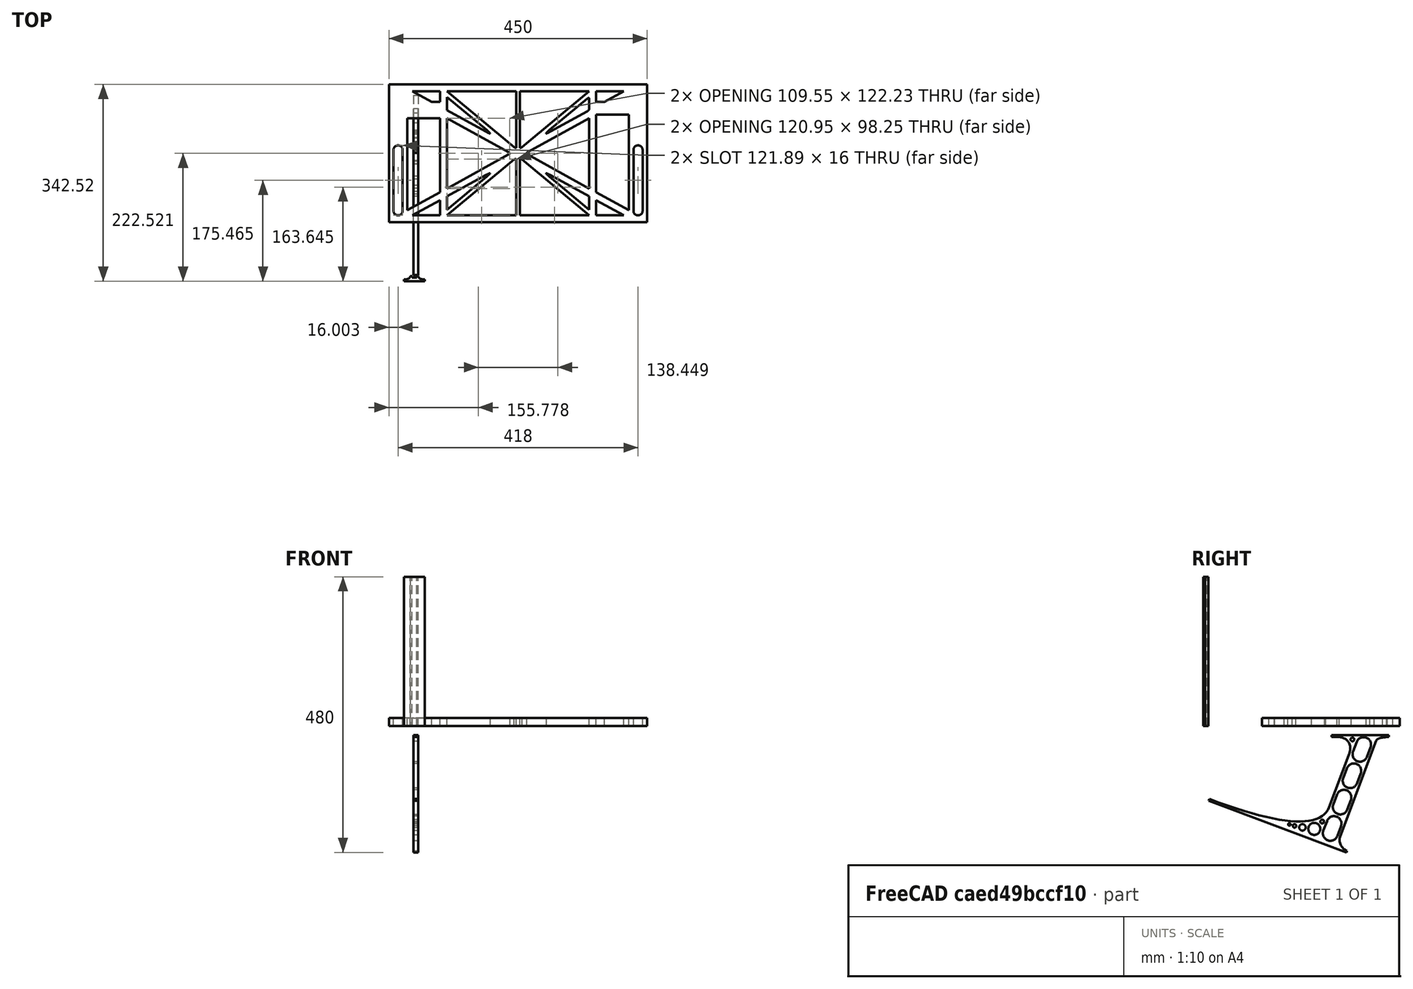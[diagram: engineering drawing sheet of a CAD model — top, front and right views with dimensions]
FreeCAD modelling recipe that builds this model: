
FCSTD DOCUMENT  (FreeCAD 0.19R0.19.2)
Label: laptopStand071
License: All rights reserved
LicenseURL: http://en.wikipedia.org/wiki/All_rights_reserved
objects: Sketcher::SketchObject×3, Part::Extrusion×3
note: 6 computed .brp shape members not serialized (recipe doc carries the construction recipe); baked Part::Feature solids carry a one-line shape summary decoded from their .brp

FEATURE [Sketcher::SketchObject] Sketch
  FullyConstrained = true
  sketch-geometry (136):
    g0: LineSegment StartX=-10.9272 StartY=-82.7794 StartZ=0 EndX=46.0728 EndY=-51.4823 EndZ=0
    g1: LineSegment StartX=366.073 StartY=-91.7794 StartZ=0 EndX=318.073 EndY=-65.424 EndZ=0
    g2: LineSegment StartX=-10.9272 StartY=77.3346 StartZ=0 EndX=-10.9272 EndY=-82.7794 EndZ=0
    g3: LineSegment StartX=375.073 StartY=-82.7794 StartZ=0 EndX=375.073 EndY=83.9235 EndZ=0
    g4: LineSegment StartX=-1.92719 StartY=-91.7794 StartZ=0 EndX=46.0728 EndY=-91.7794 EndZ=0
    g5: LineSegment StartX=318.073 StartY=124.221 StartZ=0 EndX=366.073 EndY=124.221 EndZ=0
    g6: LineSegment StartX=306.073 StartY=124.221 StartZ=0 EndX=189.124 EndY=27.0628 EndZ=0
    g7: LineSegment StartX=58.0728 StartY=-91.7794 StartZ=0 EndX=175.022 EndY=5.37834 EndZ=0
    g8: LineSegment StartX=58.0728 StartY=-81.8102 StartZ=0 EndX=58.0728 EndY=-58.8351 EndZ=0
    g9: LineSegment StartX=175.022 StartY=27.0628 StartZ=0 EndX=58.0728 EndY=124.221 EndZ=0
    g10: LineSegment StartX=189.124 StartY=5.37834 StartZ=0 EndX=306.073 EndY=-91.7794 EndZ=0
    g11: LineSegment StartX=306.073 StartY=77.3346 StartZ=0 EndX=306.073 EndY=-44.8935 EndZ=0
    g12: LineSegment StartX=318.073 StartY=83.9235 StartZ=0 EndX=318.073 EndY=-51.4823 EndZ=0
    g13: LineSegment StartX=306.073 StartY=-58.8351 StartZ=0 EndX=306.073 EndY=-81.8102 EndZ=0
    g14: LineSegment StartX=318.073 StartY=-51.4823 StartZ=0 EndX=375.073 EndY=-82.7794 EndZ=0
    g15: LineSegment StartX=318.073 StartY=-65.424 StartZ=0 EndX=318.073 EndY=-91.7794 EndZ=0
    g16: LineSegment StartX=318.073 StartY=-91.7794 StartZ=0 EndX=366.073 EndY=-91.7794 EndZ=0
    g17: LineSegment StartX=58.0728 StartY=-44.8935 StartZ=0 EndX=58.0728 EndY=77.3346 EndZ=0
    g18: LineSegment StartX=46.0728 StartY=-65.424 StartZ=0 EndX=-1.92719 EndY=-91.7794 EndZ=0
    g19: LineSegment StartX=46.0728 StartY=-65.424 StartZ=0 EndX=46.0728 EndY=-91.7794 EndZ=0
    g20: LineSegment StartX=58.0728 StartY=91.2763 StartZ=0 EndX=58.0728 EndY=114.251 EndZ=0
    g21: LineSegment StartX=46.0728 StartY=77.3346 StartZ=0 EndX=46.0728 EndY=-51.4823 EndZ=0
    g22: LineSegment StartX=-42.9272 StartY=136.221 StartZ=0 EndX=-42.9272 EndY=-103.779 EndZ=0
    g23: LineSegment StartX=407.073 StartY=136.221 StartZ=0 EndX=407.073 EndY=-103.779 EndZ=0
    g24: LineSegment StartX=179.022 StartY=27.0628 StartZ=0 EndX=179.022 EndY=124.221 EndZ=0
    g25: LineSegment StartX=185.124 StartY=27.0628 StartZ=0 EndX=185.124 EndY=124.221 EndZ=0
    g26: ArcOfCircle CenterX=-26.9272 CenterY=22.1087 CenterZ=0 NormalX=0 NormalY=0 NormalZ=1 AngleXU=0 Radius=8 StartAngle=1e-16 EndAngle=3.14159
    g27: ArcOfCircle CenterX=-26.9272 CenterY=-83.7794 CenterZ=0 NormalX=0 NormalY=0 NormalZ=1 AngleXU=0 Radius=8 StartAngle=3.14159 EndAngle=6.28319
    g28: LineSegment StartX=-34.9272 StartY=22.1087 StartZ=0 EndX=-34.9272 EndY=-83.7794 EndZ=0
    g29: LineSegment StartX=-18.9272 StartY=22.1087 StartZ=0 EndX=-18.9272 EndY=-83.7794 EndZ=0
    g30: LineSegment StartX=185.124 StartY=-91.7794 StartZ=0 EndX=306.073 EndY=-91.7794 EndZ=0
    g31: LineSegment StartX=179.022 StartY=-91.7794 StartZ=0 EndX=58.0728 EndY=-91.7794 EndZ=0
    g32: LineSegment StartX=306.073 StartY=124.221 StartZ=0 EndX=185.124 EndY=124.221 EndZ=0
    g33: LineSegment StartX=179.022 StartY=124.221 StartZ=0 EndX=58.0728 EndY=124.221 EndZ=0
    g34: ArcOfCircle CenterX=391.073 CenterY=22.1087 CenterZ=0 NormalX=0 NormalY=0 NormalZ=1 AngleXU=0 Radius=8 StartAngle=-4.4e-15 EndAngle=3.14159
    g35: LineSegment StartX=399.073 StartY=22.1087 StartZ=0 EndX=399.073 EndY=-83.7794 EndZ=0
    g36: LineSegment StartX=383.073 StartY=22.1087 StartZ=0 EndX=383.073 EndY=-83.7794 EndZ=0
    g37: ArcOfCircle CenterX=391.073 CenterY=-83.7794 CenterZ=0 NormalX=0 NormalY=0 NormalZ=1 AngleXU=0 Radius=8 StartAngle=3.14159 EndAngle=6.28319
    g38: Circle CenterX=175.022 CenterY=27.0628 CenterZ=0 NormalX=0 NormalY=0 NormalZ=1 AngleXU=0 Radius=1
    g39: Circle CenterX=179.022 CenterY=24.8665 CenterZ=0 NormalX=0 NormalY=0 NormalZ=1 AngleXU=0 Radius=1
    g40: Circle CenterX=179.022 CenterY=27.0628 CenterZ=0 NormalX=0 NormalY=0 NormalZ=1 AngleXU=0 Radius=1
    g41: BSplineCurve PolesCount=3 KnotsCount=2 Degree=2 IsPeriodic=0
    g42: GeomPoint X=175.022 Y=27.0628 Z=0
    g43: GeomPoint X=179.022 Y=27.0628 Z=0
    g44: Circle CenterX=189.124 CenterY=27.0628 CenterZ=0 NormalX=0 NormalY=0 NormalZ=1 AngleXU=0 Radius=1
    g45: Circle CenterX=185.124 CenterY=24.8665 CenterZ=0 NormalX=0 NormalY=0 NormalZ=1 AngleXU=0 Radius=1
    g46: Circle CenterX=185.124 CenterY=27.0628 CenterZ=0 NormalX=0 NormalY=0 NormalZ=1 AngleXU=0 Radius=1
    g47: BSplineCurve PolesCount=3 KnotsCount=2 Degree=2 IsPeriodic=0
    g48: GeomPoint X=189.124 Y=27.0628 Z=0
    g49: GeomPoint X=185.124 Y=27.0628 Z=0
    g50: Circle CenterX=175.022 CenterY=5.37834 CenterZ=0 NormalX=0 NormalY=0 NormalZ=1 AngleXU=0 Radius=1
    g51: Circle CenterX=179.022 CenterY=7.57463 CenterZ=0 NormalX=0 NormalY=0 NormalZ=1 AngleXU=0 Radius=1
    g52: Circle CenterX=179.022 CenterY=5.34704 CenterZ=0 NormalX=0 NormalY=0 NormalZ=1 AngleXU=0 Radius=1
    g53: BSplineCurve PolesCount=3 KnotsCount=2 Degree=2 IsPeriodic=0
    g54: GeomPoint X=175.022 Y=5.37834 Z=0
    g55: GeomPoint X=179.022 Y=5.34704 Z=0
    g56: Circle CenterX=189.124 CenterY=5.37834 CenterZ=0 NormalX=0 NormalY=0 NormalZ=1 AngleXU=0 Radius=1
    g57: Circle CenterX=185.124 CenterY=7.57463 CenterZ=0 NormalX=0 NormalY=0 NormalZ=1 AngleXU=0 Radius=1
    g58: Circle CenterX=185.124 CenterY=5.34704 CenterZ=0 NormalX=0 NormalY=0 NormalZ=1 AngleXU=0 Radius=1
    g59: BSplineCurve PolesCount=3 KnotsCount=2 Degree=2 IsPeriodic=0
    g60: GeomPoint X=189.124 Y=5.37834 Z=0
    g61: GeomPoint X=185.124 Y=5.34704 Z=0
    g62: LineSegment StartX=179.022 StartY=5.34704 StartZ=0 EndX=179.022 EndY=-91.7794 EndZ=0
    g63: LineSegment StartX=185.124 StartY=-91.7794 StartZ=0 EndX=185.124 EndY=5.34704 EndZ=0
    g64: Circle CenterX=165.871 CenterY=18.1458 CenterZ=0 NormalX=0 NormalY=0 NormalZ=1 AngleXU=0 Radius=1
    g65: Circle CenterX=169.377 CenterY=16.2206 CenterZ=0 NormalX=0 NormalY=0 NormalZ=1 AngleXU=0 Radius=1
    g66: Circle CenterX=165.871 CenterY=14.2954 CenterZ=0 NormalX=0 NormalY=0 NormalZ=1 AngleXU=0 Radius=1
    g67: BSplineCurve PolesCount=3 KnotsCount=2 Degree=2 IsPeriodic=0
    g68: GeomPoint X=165.871 Y=18.1458 Z=0
    g69: GeomPoint X=165.871 Y=14.2954 Z=0
    g70: Circle CenterX=198.275 CenterY=18.1458 CenterZ=0 NormalX=0 NormalY=0 NormalZ=1 AngleXU=0 Radius=1
    g71: Circle CenterX=194.768 CenterY=16.2206 CenterZ=0 NormalX=0 NormalY=0 NormalZ=1 AngleXU=0 Radius=1
    g72: Circle CenterX=198.275 CenterY=14.2954 CenterZ=0 NormalX=0 NormalY=0 NormalZ=1 AngleXU=0 Radius=1
    g73: BSplineCurve PolesCount=3 KnotsCount=2 Degree=2 IsPeriodic=0
    g74: GeomPoint X=198.275 Y=18.1458 Z=0
    g75: GeomPoint X=198.275 Y=14.2954 Z=0
    g76: LineSegment StartX=165.871 StartY=18.1458 StartZ=0 EndX=58.0728 EndY=77.3346 EndZ=0
    g77: LineSegment StartX=58.0728 StartY=-44.8935 StartZ=0 EndX=165.871 EndY=14.2954 EndZ=0
    g78: LineSegment StartX=198.275 StartY=18.1458 StartZ=0 EndX=306.073 EndY=77.3346 EndZ=0
    g79: LineSegment StartX=198.275 StartY=14.2954 StartZ=0 EndX=306.073 EndY=-44.8935 EndZ=0
    g80: LineSegment StartX=407.073 StartY=-103.779 StartZ=0 EndX=-42.9272 EndY=-103.779 EndZ=0
    g81: LineSegment StartX=407.073 StartY=136.221 StartZ=0 EndX=-42.9272 EndY=136.221 EndZ=0
    g82: LineSegment StartX=46.0728 StartY=77.3346 StartZ=0 EndX=-10.9272 EndY=77.3346 EndZ=0
    g83: LineSegment StartX=46.0728 StartY=105.865 StartZ=0 EndX=31.5028 EndY=105.865 EndZ=0
    g84: LineSegment StartX=46.0728 StartY=124.221 StartZ=0 EndX=46.0728 EndY=105.865 EndZ=0
    g85: LineSegment StartX=-1.92719 StartY=124.221 StartZ=0 EndX=31.5028 EndY=105.865 EndZ=0
    g86: LineSegment StartX=46.0728 StartY=124.221 StartZ=0 EndX=-1.92719 EndY=124.221 EndZ=0
    g87: LineSegment StartX=318.073 StartY=83.9235 StartZ=0 EndX=375.073 EndY=83.9235 EndZ=0
    g88: LineSegment StartX=318.073 StartY=105.865 StartZ=0 EndX=332.643 EndY=105.865 EndZ=0
    g89: LineSegment StartX=332.643 StartY=105.865 StartZ=0 EndX=366.073 EndY=124.221 EndZ=0
    g90: LineSegment StartX=318.073 StartY=124.221 StartZ=0 EndX=318.073 EndY=105.865 EndZ=0
    g91: Circle CenterX=125.607 CenterY=54.1951 CenterZ=0 NormalX=0 NormalY=0 NormalZ=1 AngleXU=0 Radius=1
    g92: Circle CenterX=139.632 CenterY=46.4944 CenterZ=0 NormalX=0 NormalY=0 NormalZ=1 AngleXU=0 Radius=1
    g93: Circle CenterX=127.325 CenterY=56.7187 CenterZ=0 NormalX=0 NormalY=0 NormalZ=1 AngleXU=0 Radius=1
    g94: BSplineCurve PolesCount=3 KnotsCount=2 Degree=2 IsPeriodic=0
    g95: GeomPoint X=125.607 Y=54.1951 Z=0
    g96: GeomPoint X=127.325 Y=56.7187 Z=0
    g97: LineSegment StartX=127.325 StartY=56.7187 StartZ=0 EndX=58.0728 EndY=114.251 EndZ=0
    g98: LineSegment StartX=58.0728 StartY=91.2763 StartZ=0 EndX=125.607 EndY=54.1951 EndZ=0
    g99: Circle CenterX=236.821 CenterY=56.7187 CenterZ=0 NormalX=0 NormalY=0 NormalZ=1 AngleXU=0 Radius=1
    g100: Circle CenterX=224.513 CenterY=46.4944 CenterZ=0 NormalX=0 NormalY=0 NormalZ=1 AngleXU=0 Radius=1
    g101: Circle CenterX=238.538 CenterY=54.1951 CenterZ=0 NormalX=0 NormalY=0 NormalZ=1 AngleXU=0 Radius=1
    g102: BSplineCurve PolesCount=3 KnotsCount=2 Degree=2 IsPeriodic=0
    g103: GeomPoint X=236.821 Y=56.7187 Z=0
    g104: GeomPoint X=238.538 Y=54.1951 Z=0
    g105: Circle CenterX=238.538 CenterY=-21.7539 CenterZ=0 NormalX=0 NormalY=0 NormalZ=1 AngleXU=0 Radius=1
    g106: Circle CenterX=224.513 CenterY=-14.0532 CenterZ=0 NormalX=0 NormalY=0 NormalZ=1 AngleXU=0 Radius=1
    g107: Circle CenterX=236.821 CenterY=-24.2775 CenterZ=0 NormalX=0 NormalY=0 NormalZ=1 AngleXU=0 Radius=1
    g108: BSplineCurve PolesCount=3 KnotsCount=2 Degree=2 IsPeriodic=0
    g109: GeomPoint X=238.538 Y=-21.7539 Z=0
    g110: GeomPoint X=236.821 Y=-24.2775 Z=0
    g111: LineSegment StartX=238.538 StartY=-21.7539 StartZ=0 EndX=306.073 EndY=-58.8351 EndZ=0
    g112: LineSegment StartX=236.821 StartY=-24.2775 StartZ=0 EndX=306.073 EndY=-81.8102 EndZ=0
    g113: Circle CenterX=125.607 CenterY=-21.7539 CenterZ=0 NormalX=0 NormalY=0 NormalZ=1 AngleXU=0 Radius=1
    g114: Circle CenterX=139.632 CenterY=-14.0532 CenterZ=0 NormalX=0 NormalY=0 NormalZ=1 AngleXU=0 Radius=1
    g115: Circle CenterX=127.325 CenterY=-24.2775 CenterZ=0 NormalX=0 NormalY=0 NormalZ=1 AngleXU=0 Radius=1
    g116: BSplineCurve PolesCount=3 KnotsCount=2 Degree=2 IsPeriodic=0
    g117: GeomPoint X=125.607 Y=-21.7539 Z=0
    g118: GeomPoint X=127.325 Y=-24.2775 Z=0
    g119: LineSegment StartX=125.607 StartY=-21.7539 StartZ=0 EndX=58.0728 EndY=-58.8351 EndZ=0
    g120: LineSegment StartX=127.325 StartY=-24.2775 StartZ=0 EndX=58.0728 EndY=-81.8102 EndZ=0
    g121: Circle CenterX=302.996 CenterY=111.695 CenterZ=0 NormalX=0 NormalY=0 NormalZ=1 AngleXU=0 Radius=1
    g122: Circle CenterX=306.073 CenterY=114.251 CenterZ=0 NormalX=0 NormalY=0 NormalZ=1 AngleXU=0 Radius=1
    g123: Circle CenterX=306.073 CenterY=110.251 CenterZ=0 NormalX=0 NormalY=0 NormalZ=1 AngleXU=0 Radius=1
    g124: BSplineCurve PolesCount=3 KnotsCount=2 Degree=2 IsPeriodic=0
    g125: GeomPoint X=302.996 Y=111.695 Z=0
    g126: GeomPoint X=306.073 Y=110.251 Z=0
    g127: Circle CenterX=306.073 CenterY=95.2763 CenterZ=0 NormalX=0 NormalY=0 NormalZ=1 AngleXU=0 Radius=1
    g128: Circle CenterX=306.073 CenterY=91.2763 CenterZ=0 NormalX=0 NormalY=0 NormalZ=1 AngleXU=0 Radius=1
    g129: Circle CenterX=302.567 CenterY=89.3511 CenterZ=0 NormalX=0 NormalY=0 NormalZ=1 AngleXU=0 Radius=1
    g130: BSplineCurve PolesCount=3 KnotsCount=2 Degree=2 IsPeriodic=0
    g131: GeomPoint X=306.073 Y=95.2763 Z=0
    g132: GeomPoint X=302.567 Y=89.3511 Z=0
    g133: LineSegment StartX=306.073 StartY=110.251 StartZ=0 EndX=306.073 EndY=95.2763 EndZ=0
    g134: LineSegment StartX=302.996 StartY=111.695 StartZ=0 EndX=236.821 EndY=56.7187 EndZ=0
    g135: LineSegment StartX=238.538 StartY=54.1951 StartZ=0 EndX=302.567 EndY=89.3511 EndZ=0
  constraints (243):
    c: Horizontal(g4)
    c: Horizontal(g5)
    c: Tangent(g11,g13)
    c: Coincident(g12,g14)
    c: Coincident(g15,g1)
    c: Tangent(g12,g15)
    c: Tangent(g8,g17)
    c: Coincident(g19,g18)
    c: Coincident(g0,g21)
    c: Tangent(g17,g20)
    c: Block(g9)
    c: Block(g6)
    c: Block(g14)
    c: Block(g3)
    c: Block(g13)
    c: Block(g1)
    c: Block(g15)
    c: Block(g10)
    c: Block(g7)
    c: Block(g19)
    c: Block(g18)
    c: Block(g0)
    c: Block(g2)
    c: Block(g20)
    c: Block(g11)
    c: Block(g5)
    c: Block(g16)
    c: Block(g4)
    c: Vertical(g22)
    c: Vertical(g23)
    c: Block(g23)
    c: Block(g22)
    c: Vertical(g24)
    c: Vertical(g25)
    c: Block(g24)
    c: Block(g25)
    c: Tangent(g26,g29) = 1.5708
    c: Tangent(g26,g28) = -1.5708
    c: Tangent(g28,g27) = -1.5708
    c: Tangent(g29,g27) = 1.5708
    c: Vertical(g28)
    c: Equal(g26,g27)
    c: Block(g29)
    c: Block(g28)
    c: Coincident(g30,g10)
    c: Horizontal(g30)
    c: Coincident(g31,g7)
    c: Horizontal(g31)
    c: Coincident(g32,g6)
    c: Coincident(g32,g25)
    c: Horizontal(g32)
    c: Coincident(g33,g24)
    c: Coincident(g33,g9)
    c: Horizontal(g33)
    c: Tangent(g34,g35) = 1.5708
    c: Tangent(g35,g37) = 1.5708
    c: Equal(g34,g37)
    c: Coincident(g36,g34)
    c: Coincident(g36,g37)
    c: Block(g35)
    c: Block(g36)
    c: Coincident(g41,g9)
    c: Weight(g38) = 1
    c: Equal(g38,g39)
    c: Equal(g38,g40)
    c: Coincident(g41,g24)
    c: InternalAlignment(g38,g41)
    c: InternalAlignment(g39,g41)
    c: InternalAlignment(g40,g41)
    c: InternalAlignment(g42,g41)
    c: InternalAlignment(g43,g41)
    c: Coincident(g47,g6)
    c: Weight(g44) = 1
    c: Equal(g44,g45)
    c: Equal(g44,g46)
    c: Coincident(g47,g25)
    c: InternalAlignment(g44,g47)
    c: InternalAlignment(g45,g47)
    c: InternalAlignment(g46,g47)
    c: InternalAlignment(g48,g47)
    c: InternalAlignment(g49,g47)
    c: Block(g47)
    c: Block(g41)
    c: Coincident(g53,g7)
    c: Weight(g50) = 1
    c: Equal(g50,g51)
    c: Equal(g50,g52)
    c: InternalAlignment(g50,g53)
    c: InternalAlignment(g51,g53)
    c: InternalAlignment(g52,g53)
    c: InternalAlignment(g54,g53)
    c: InternalAlignment(g55,g53)
    c: Weight(g56) = 1
    c: Equal(g56,g57)
    c: Equal(g56,g58)
    c: InternalAlignment(g56,g59)
    c: InternalAlignment(g57,g59)
    c: InternalAlignment(g58,g59)
    c: InternalAlignment(g60,g59)
    c: InternalAlignment(g61,g59)
    c: Block(g59)
    c: Block(g53)
    c: Coincident(g62,g53)
    c: Coincident(g62,g31)
    c: Vertical(g62)
    c: Coincident(g63,g30)
    c: Coincident(g63,g59)
    c: Vertical(g63)
    c: Weight(g64) = 1
    c: Equal(g64,g65)
    c: Equal(g64,g66)
    c: InternalAlignment(g64,g67)
    c: InternalAlignment(g65,g67)
    c: InternalAlignment(g66,g67)
    c: InternalAlignment(g68,g67)
    c: InternalAlignment(g69,g67)
    c: Weight(g70) = 1
    c: Equal(g70,g71)
    c: Equal(g70,g72)
    c: InternalAlignment(g70,g73)
    c: InternalAlignment(g71,g73)
    c: InternalAlignment(g72,g73)
    c: InternalAlignment(g74,g73)
    c: InternalAlignment(g75,g73)
    c: Block(g67)
    c: Block(g73)
    c: Coincident(g76,g67)
    c: Coincident(g76,g17)
    c: Coincident(g77,g17)
    c: Coincident(g77,g67)
    c: Coincident(g78,g73)
    c: Coincident(g78,g11)
    c: Coincident(g79,g73)
    c: Coincident(g79,g11)
    c: Block(g17)
    c: Coincident(g80,g23)
    c: Coincident(g80,g22)
    c: Horizontal(g80)
    c: Distance(g80) = 450
    c: Coincident(g81,g23)
    c: Coincident(g81,g22)
    c: Horizontal(g81)
    c: Horizontal(g82)
    c: Coincident(g21,g82)
    c: Horizontal(g83)
    c: Vertical(g84)
    c: Block(g84)
    c: Block(g83)
    c: Block(g82)
    c: Distance(g84) = 18.3554
    c: Coincident(g86,g84)
    c: Coincident(g86,g85)
    c: Horizontal(g86)
    c: Block(g86)
    c: Block(g85)
    c: Coincident(g83,g85)
    c: Coincident(g2,g82)
    c: Coincident(g87,g12)
    c: Horizontal(g87)
    c: Horizontal(g88)
    c: Block(g87)
    c: Coincident(g89,g5)
    c: Coincident(g90,g5)
    c: Coincident(g90,g88)
    c: Vertical(g90)
    c: Block(g90)
    c: Coincident(g88,g89)
    c: Block(g89)
    c: Coincident(g3,g87)
    c: Weight(g91) = 1
    c: Equal(g91,g92)
    c: Equal(g91,g93)
    c: InternalAlignment(g91,g94)
    c: InternalAlignment(g92,g94)
    c: InternalAlignment(g93,g94)
    c: InternalAlignment(g95,g94)
    c: InternalAlignment(g96,g94)
    c: Block(g94)
    c: Coincident(g97,g94)
    c: Coincident(g97,g20)
    c: Coincident(g98,g20)
    c: Coincident(g98,g94)
    c: Weight(g99) = 1
    c: Equal(g99,g100)
    c: Equal(g99,g101)
    c: InternalAlignment(g99,g102)
    c: InternalAlignment(g100,g102)
    c: InternalAlignment(g101,g102)
    c: InternalAlignment(g103,g102)
    c: InternalAlignment(g104,g102)
    c: Block(g102)
    c: Weight(g105) = 1
    c: Equal(g105,g106)
    c: Equal(g105,g107)
    c: InternalAlignment(g105,g108)
    c: InternalAlignment(g106,g108)
    c: InternalAlignment(g107,g108)
    c: InternalAlignment(g109,g108)
    c: InternalAlignment(g110,g108)
    c: Block(g108)
    c: Coincident(g111,g108)
    c: Coincident(g111,g13)
    c: Coincident(g112,g108)
    c: Coincident(g112,g13)
    c: Weight(g113) = 1
    c: Equal(g113,g114)
    c: Equal(g113,g115)
    c: InternalAlignment(g113,g116)
    c: InternalAlignment(g114,g116)
    c: InternalAlignment(g115,g116)
    c: InternalAlignment(g117,g116)
    c: InternalAlignment(g118,g116)
    c: Block(g116)
    c: Coincident(g119,g116)
    c: Coincident(g119,g8)
    c: Coincident(g120,g116)
    c: Coincident(g120,g8)
    c: Block(g8)
    c: Weight(g121) = 1
    c: Equal(g121,g122)
    c: Equal(g121,g123)
    c: InternalAlignment(g121,g124)
    c: InternalAlignment(g122,g124)
    c: InternalAlignment(g123,g124)
    c: InternalAlignment(g125,g124)
    c: InternalAlignment(g126,g124)
    c: Weight(g127) = 1
    c: Equal(g127,g128)
    c: Equal(g127,g129)
    c: InternalAlignment(g127,g130)
    c: InternalAlignment(g128,g130)
    c: InternalAlignment(g129,g130)
    c: InternalAlignment(g131,g130)
    c: InternalAlignment(g132,g130)
    c: Block(g124)
    c: Block(g130)
    c: Coincident(g133,g124)
    c: Coincident(g133,g130)
    c: Vertical(g133)
    c: Coincident(g134,g124)
    c: Coincident(g134,g102)
    c: Coincident(g135,g102)
    c: Coincident(g135,g130)
FEATURE [Sketcher::SketchObject] Sketch001
  FullyConstrained = true
  MapMode = 4
  Placement = pos=(0,0,0) rot=(0.57735,0.57735,0.57735;2.0944rad)
  Support = -> [Sketch]
  sketch-geometry (46):
    g0: BSplineCurve PolesCount=3 KnotsCount=2 Degree=2 IsPeriodic=0
    g1: ArcOfCircle CenterX=73.1223 CenterY=-32.291 CenterZ=0 NormalX=0 NormalY=0 NormalZ=1 AngleXU=0 Radius=13 StartAngle=5.92268 EndAngle=9.06428
    g2: ArcOfCircle CenterX=66.7816 CenterY=-49.1439 CenterZ=0 NormalX=0 NormalY=0 NormalZ=1 AngleXU=0 Radius=13 StartAngle=2.78068 EndAngle=5.92131
    g3: ArcOfCircle CenterX=55.9263 CenterY=-78.1807 CenterZ=0 NormalX=0 NormalY=0 NormalZ=1 AngleXU=0 Radius=13 StartAngle=5.92268 EndAngle=9.06428
    g4: ArcOfCircle CenterX=49.5884 CenterY=-95.0342 CenterZ=0 NormalX=0 NormalY=0 NormalZ=1 AngleXU=0 Radius=13 StartAngle=2.78068 EndAngle=5.92131
    g5: ArcOfCircle CenterX=38.7206 CenterY=-124.067 CenterZ=0 NormalX=0 NormalY=0 NormalZ=1 AngleXU=0 Radius=13 StartAngle=5.92268 EndAngle=9.06428
    g6: ArcOfCircle CenterX=32.3875 CenterY=-140.92 CenterZ=0 NormalX=0 NormalY=0 NormalZ=1 AngleXU=0 Radius=13 StartAngle=2.78068 EndAngle=5.92131
    g7: ArcOfCircle CenterX=21.4715 CenterY=-169.934 CenterZ=0 NormalX=0 NormalY=0 NormalZ=1 AngleXU=0 Radius=13 StartAngle=5.92268 EndAngle=9.06428
    g8: ArcOfCircle CenterX=15.1336 CenterY=-186.787 CenterZ=0 NormalX=0 NormalY=0 NormalZ=1 AngleXU=0 Radius=13 StartAngle=2.78068 EndAngle=5.92131
    g9-g12: Circle x4 (B-spline internal-alignment scaffolding for g13; pole/knot coordinates omitted)
    g13: BSplineCurve PolesCount=4 KnotsCount=2 Degree=3 IsPeriodic=0
    g14: GeomPoint X=28.8094 Y=-19.0875 Z=0
    g15: GeomPoint X=47.0443 Y=-50.4712 Z=0
    g16: Circle CenterX=53.5586 CenterY=-23.2695 CenterZ=0 NormalX=0 NormalY=0 NormalZ=1 AngleXU=0 Radius=3.24518
    g17: Circle CenterX=-195.441 CenterY=-127.082 CenterZ=0 NormalX=0 NormalY=0 NormalZ=1 AngleXU=0 Radius=1
    g18: Circle CenterX=-8.24091 CenterY=-197.481 CenterZ=0 NormalX=0 NormalY=0 NormalZ=1 AngleXU=0 Radius=1
    g19: Circle CenterX=12.8789 CenterY=-141.321 CenterZ=0 NormalX=0 NormalY=0 NormalZ=1 AngleXU=0 Radius=1
    g20: BSplineCurve PolesCount=3 KnotsCount=2 Degree=2 IsPeriodic=0
    g21: GeomPoint X=-195.441 Y=-127.082 Z=0
    g22: GeomPoint X=12.8789 Y=-141.321 Z=0
    g23: Circle CenterX=-12.8016 CenterY=-179.036 CenterZ=0 NormalX=0 NormalY=0 NormalZ=1 AngleXU=0 Radius=10.5072
    g24: Circle CenterX=0.933922 CenterY=-166.43 CenterZ=0 NormalX=0 NormalY=0 NormalZ=1 AngleXU=0 Radius=3.26661
    g25: Circle CenterX=-33.5518 CenterY=-176.44 CenterZ=0 NormalX=0 NormalY=0 NormalZ=1 AngleXU=0 Radius=5.64388
    g26: Circle CenterX=-47.2366 CenterY=-173.859 CenterZ=0 NormalX=0 NormalY=0 NormalZ=1 AngleXU=0 Radius=3.01653
    g27: Circle CenterX=-56.2595 CenterY=-171.456 CenterZ=0 NormalX=0 NormalY=0 NormalZ=1 AngleXU=0 Radius=2.12826
    g28: ArcOfCircle CenterX=51.2151 CenterY=-198.473 CenterZ=0 NormalX=0 NormalY=0 NormalZ=1 AngleXU=0 Radius=20 StartAngle=2.78189 EndAngle=4.35269
    g29: LineSegment StartX=32.4951 StartY=-191.433 StartZ=0 EndX=94.6578 EndY=-26.1352 EndZ=0
    g30: LineSegment StartX=43.1192 StartY=-220.001 StartZ=0 EndX=-196.497 EndY=-129.89 EndZ=0
    g31: LineSegment StartX=43.1192 StartY=-220.001 StartZ=0 EndX=44.1752 EndY=-217.193 EndZ=0
    g32: LineSegment StartX=117.223 StartY=-19.0875 StartZ=0 EndX=117.223 EndY=-16.0875 EndZ=0
    g33: LineSegment StartX=117.223 StartY=-16.0875 StartZ=0 EndX=17.2232 EndY=-16.0875 EndZ=0
    g34: LineSegment StartX=17.2232 StartY=-16.0875 StartZ=0 EndX=17.2232 EndY=-19.0875 EndZ=0
    g35: LineSegment StartX=28.8094 StartY=-19.0875 StartZ=0 EndX=17.2232 EndY=-19.0875 EndZ=0
    g36: LineSegment StartX=47.0443 StartY=-50.4712 StartZ=0 EndX=12.8789 EndY=-141.321 EndZ=0
    g37: LineSegment StartX=-195.441 StartY=-127.082 StartZ=0 EndX=-196.497 EndY=-129.89 EndZ=0
    g38: LineSegment StartX=85.2866 StartY=-36.8766 StartZ=0 EndX=78.9396 EndY=-53.7463 EndZ=0
    g39: LineSegment StartX=60.9579 StartY=-27.7053 StartZ=0 EndX=54.6191 EndY=-44.5532 EndZ=0
    g40: LineSegment StartX=68.0907 StartY=-82.7664 StartZ=0 EndX=61.7465 EndY=-99.6365 EndZ=0
    g41: LineSegment StartX=43.7619 StartY=-73.595 StartZ=0 EndX=37.426 EndY=-90.4435 EndZ=0
    g42: LineSegment StartX=50.885 StartY=-128.652 StartZ=0 EndX=44.5456 EndY=-145.522 EndZ=0
    g43: LineSegment StartX=26.5562 StartY=-119.481 StartZ=0 EndX=20.2251 EndY=-136.329 EndZ=0
    g44: LineSegment StartX=9.3071 StartY=-165.349 StartZ=0 EndX=2.97115 EndY=-182.197 EndZ=0
    g45: LineSegment StartX=33.6358 StartY=-174.52 StartZ=0 EndX=27.2917 EndY=-191.39 EndZ=0
  constraints (71):
    c: Block(g0)
    c: Block(g1)
    c: Block(g2)
    c: Block(g4)
    c: Block(g3)
    c: Block(g6)
    c: Block(g5)
    c: Block(g8)
    c: Block(g7)
    c: Weight(g9) = 1
    c: Equal(g9,g10)
    c: Equal(g9,g11)
    c: Equal(g9,g12)
    c: InternalAlignment(g9-g12 -> g13) x4
    c: InternalAlignment(g14,g13)
    c: InternalAlignment(g15,g13)
    c: Block(g16)
    c: Weight(g17) = 1
    c: Equal(g17,g18)
    c: Equal(g17,g19)
    c: InternalAlignment(g17,g20)
    c: InternalAlignment(g18,g20)
    c: InternalAlignment(g19,g20)
    c: InternalAlignment(g21,g20)
    c: InternalAlignment(g22,g20)
    c: Block(g20)
    c: Block(g23)
    c: Block(g24)
    c: Block(g25)
    c: Block(g26)
    c: Block(g27)
    c: Block(g28)
    c: Coincident(g29,g28)
    c: Coincident(g29,g0)
    c: Block(g13)
    c: Coincident(g31,g30)
    c: Coincident(g31,g28)
    c: Block(g31)
    c: Coincident(g32,g0)
    c: Vertical(g32)
    c: Coincident(g33,g32)
    c: Horizontal(g33)
    c: Coincident(g34,g33)
    c: Vertical(g34)
    c: Block(g33)
    c: Coincident(g35,g13)
    c: Coincident(g35,g34)
    c: Horizontal(g35)
    c: Coincident(g36,g13)
    c: Coincident(g36,g20)
    c: Coincident(g37,g20)
    c: Coincident(g37,g30)
    c: Block(g30)
    c: Coincident(g38,g1)
    c: Coincident(g38,g2)
    c: Coincident(g39,g1)
    c: Coincident(g39,g2)
    c: Coincident(g40,g3)
    c: Coincident(g40,g4)
    c: Coincident(g41,g3)
    c: Coincident(g41,g4)
    c: Coincident(g42,g5)
    c: Coincident(g42,g6)
    c: Coincident(g43,g5)
    c: Coincident(g43,g6)
    c: Coincident(g44,g7)
    c: Coincident(g44,g8)
    c: Coincident(g45,g7)
    c: Coincident(g45,g8)
    c: Distance(g30) = 256
    c: Distance(g33) = 100
FEATURE [Part::Extrusion] Extrude002
  Base = -> Sketch001
  Dir = (1,0,0)
  DirMode = 2
  FaceMakerClass = Part::FaceMakerBullseye
  LengthFwd = 8
  LengthRev = 0
  Solid = true
  Symmetric = false
FEATURE [Sketcher::SketchObject] Sketch002
  FullyConstrained = true
  sketch-geometry (20):
    g0: LineSegment StartX=-2.77179 StartY=-200.304 StartZ=0 EndX=5.22821 EndY=-200.304 EndZ=0
    g1: LineSegment StartX=5.22821 StartY=-200.304 StartZ=0 EndX=5.22821 EndY=-197.304 EndZ=0
    g2: LineSegment StartX=-2.77179 StartY=-200.304 StartZ=0 EndX=-2.77179 EndY=-197.304 EndZ=0
    g3: LineSegment StartX=5.22821 StartY=-197.304 StartZ=0 EndX=8.22821 EndY=-197.304 EndZ=0
    g4: LineSegment StartX=-2.77179 StartY=-197.304 StartZ=0 EndX=-5.77179 EndY=-197.304 EndZ=0
    g5: LineSegment StartX=19.2282 StartY=-203.304 StartZ=0 EndX=19.2282 EndY=-206.304 EndZ=0
    g6: LineSegment StartX=-16.7718 StartY=-203.304 StartZ=0 EndX=-16.7718 EndY=-206.304 EndZ=0
    g7: LineSegment StartX=-16.7718 StartY=-206.304 StartZ=0 EndX=19.2282 EndY=-206.304 EndZ=0
    g8: Circle CenterX=-16.7718 CenterY=-203.304 CenterZ=0 NormalX=0 NormalY=0 NormalZ=1 AngleXU=0 Radius=1
    g9: Circle CenterX=-5.77179 CenterY=-203.304 CenterZ=0 NormalX=0 NormalY=0 NormalZ=1 AngleXU=0 Radius=1
    g10: Circle CenterX=-5.77179 CenterY=-197.304 CenterZ=0 NormalX=0 NormalY=0 NormalZ=1 AngleXU=0 Radius=1
    g11: BSplineCurve PolesCount=3 KnotsCount=2 Degree=2 IsPeriodic=0
    g12: GeomPoint X=-16.7718 Y=-203.304 Z=0
    g13: GeomPoint X=-5.77179 Y=-197.304 Z=0
    g14: Circle CenterX=19.2282 CenterY=-203.304 CenterZ=0 NormalX=0 NormalY=0 NormalZ=1 AngleXU=0 Radius=1
    g15: Circle CenterX=8.22821 CenterY=-203.304 CenterZ=0 NormalX=0 NormalY=0 NormalZ=1 AngleXU=0 Radius=1
    g16: Circle CenterX=8.22821 CenterY=-197.304 CenterZ=0 NormalX=0 NormalY=0 NormalZ=1 AngleXU=0 Radius=1
    g17: BSplineCurve PolesCount=3 KnotsCount=2 Degree=2 IsPeriodic=0
    g18: GeomPoint X=19.2282 Y=-203.304 Z=0
    g19: GeomPoint X=8.22821 Y=-197.304 Z=0
  constraints (41):
    c: Horizontal(g0)
    c: Distance(g0) = 8
    c: Coincident(g1,g0)
    c: Vertical(g1)
    c: Distance(g1) = 3
    c: Coincident(g2,g0)
    c: Vertical(g2)
    c: Distance(g2) = 3
    c: Coincident(g3,g1)
    c: Horizontal(g3)
    c: Distance(g3) = 3
    c: Coincident(g4,g2)
    c: Horizontal(g4)
    c: Distance(g4) = 3
    c: Vertical(g5)
    c: Vertical(g6)
    c: Coincident(g7,g6)
    c: Coincident(g7,g5)
    c: Weight(g8) = 1
    c: Equal(g8,g9)
    c: Equal(g8,g10)
    c: Coincident(g11,g4)
    c: InternalAlignment(g8,g11)
    c: InternalAlignment(g9,g11)
    c: InternalAlignment(g10,g11)
    c: InternalAlignment(g12,g11)
    c: InternalAlignment(g13,g11)
    c: Coincident(g17,g5)
    c: Weight(g14) = 1
    c: Equal(g14,g15)
    c: Equal(g14,g16)
    c: Coincident(g17,g3)
    c: InternalAlignment(g14,g17)
    c: InternalAlignment(g15,g17)
    c: InternalAlignment(g16,g17)
    c: InternalAlignment(g18,g17)
    c: InternalAlignment(g19,g17)
    c: Block(g7)
    c: Block(g17)
    c: Block(g11)
    c: Block(g6)
FEATURE [Part::Extrusion] Extrude003
  Base = -> Sketch002
  Dir = (0,0,1)
  DirMode = 2
  FaceMakerClass = Part::FaceMakerBullseye
  LengthFwd = 260
  LengthRev = 0
  Solid = true
  Symmetric = false
FEATURE [Part::Extrusion] Extrude
  Base = -> Sketch
  Dir = (0,0,1)
  DirMode = 2
  FaceMakerClass = Part::FaceMakerBullseye
  LengthFwd = 14
  LengthRev = 0
  Solid = true
  Symmetric = false
